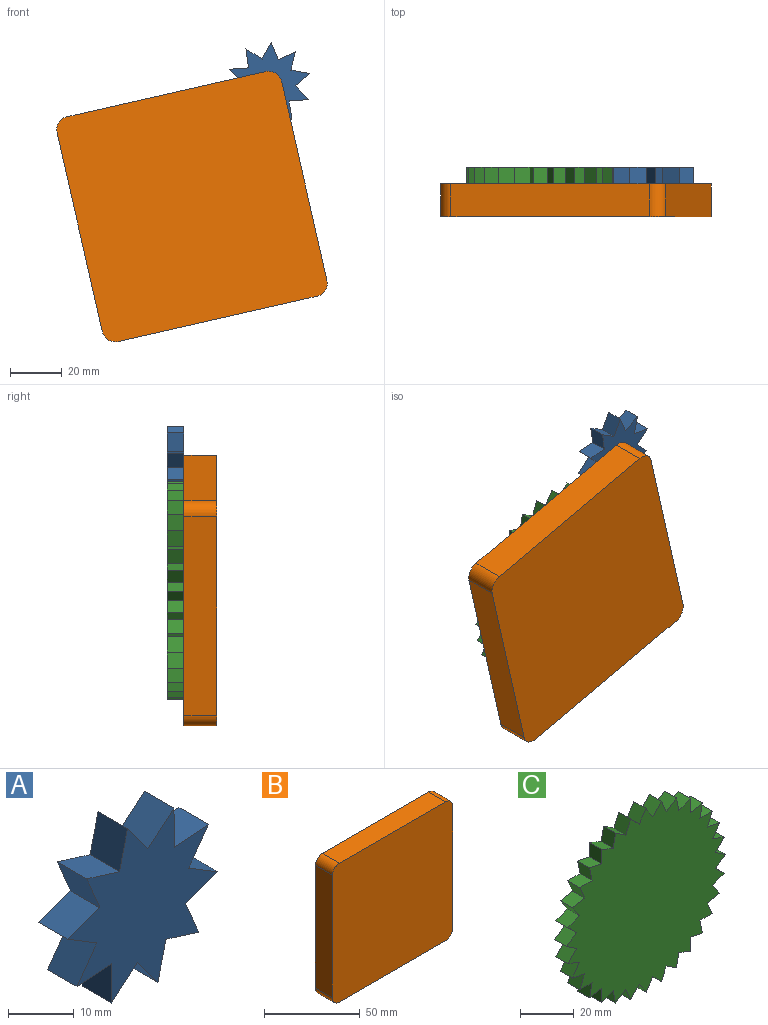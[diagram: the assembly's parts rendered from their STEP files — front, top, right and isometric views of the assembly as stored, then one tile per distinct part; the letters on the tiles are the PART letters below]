
ASSEMBLY  parts=3 mates=2
PART A: 22 faces, bbox 32.4x6.4x31.9 mm
  f0: plane 7.34x6.35mm, normal (0.08,0,-1), area 46.8mm2, adj f1,f19,f20,f21
  f1: plane 7.37x6.35mm, normal (-1,0,-0.01), area 46.8mm2, adj f0,f2,f20,f21
  f2: plane 6.35x5.61mm, normal (0.65,0,-0.76), area 46.8mm2, adj f1,f3,f20,f21
  f3: plane 6.35x5.9mm, normal (-0.8,0,-0.6), area 46.8mm2, adj f2,f4,f20,f21
  f4: plane 7.16x6.35mm, normal (0.97,0,-0.23), area 46.8mm2, adj f3,f5,f20,f21
  f5: plane 7.04x6.35mm, normal (-0.3,0,-0.96), area 46.8mm2, adj f4,f6,f20,f21
  f6: plane 6.81x6.35mm, normal (0.92,0,0.38), area 46.8mm2, adj f5,f7,f20,f21
  f7: plane 6.98x6.35mm, normal (0.32,0,-0.95), area 46.8mm2, adj f6,f8,f20,f21
  f8: plane 6.35x6.28mm, normal (0.52,0,0.85), area 46.8mm2, adj f7,f9,f20,f21
  f9: plane 6.35x6.02mm, normal (0.82,0,-0.58), area 46.8mm2, adj f8,f10,f20,f21
  f10: plane 7.34x6.35mm, normal (-0.08,0,1), area 46.8mm2, adj f9,f11,f20,f21
  f11: plane 7.37x6.35mm, normal (1,0,0.01), area 46.8mm2, adj f10,f12,f20,f21
  f12: plane 6.35x5.61mm, normal (-0.65,0,0.76), area 46.8mm2, adj f11,f13,f20,f21
  f13: plane 6.35x5.9mm, normal (0.8,0,0.6), area 46.8mm2, adj f12,f14,f20,f21
  f14: plane 7.16x6.35mm, normal (-0.97,0,0.23), area 46.8mm2, adj f13,f15,f20,f21
  f15: plane 7.04x6.35mm, normal (0.3,0,0.96), area 46.8mm2, adj f14,f16,f20,f21
  f16: plane 6.81x6.35mm, normal (-0.92,0,-0.38), area 46.8mm2, adj f15,f17,f20,f21
  f17: plane 6.98x6.35mm, normal (-0.32,0,0.95), area 46.8mm2, adj f16,f18,f20,f21
  f18: plane 6.35x6.28mm, normal (-0.52,0,-0.85), area 46.8mm2, adj f17,f19,f20,f21
  f19: plane 6.35x6.02mm, normal (-0.82,0,0.58), area 46.8mm2, adj f0,f18,f20,f21
  f20: plane 32.4x31.94mm, normal (0,-1,0), area 510.3mm2, adj f0,f1,f2,f3,f4,f5,f6,f7
  f21: plane 32.4x31.94mm, normal (0,1,0), area 510.3mm2, adj f0,f1,f2,f3,f4,f5,f6,f7
PART B: 10 faces, bbox 88.9x12.7x88.9 mm
  f0: plane 78.74x12.7mm, normal (-1,0,0), area 1000mm2, adj f4,f5,f6,f8
  f1: plane 78.74x12.7mm, normal (0,0,-1), area 1000mm2, adj f4,f5,f8,f9
  f2: plane 78.74x12.7mm, normal (1,0,0), area 1000mm2, adj f4,f5,f7,f9
  f3: plane 78.74x12.7mm, normal (0,0,1), area 1000mm2, adj f4,f5,f6,f7
  f4: plane 88.9x88.9mm, normal (0,-1,0), area 7881.1mm2, adj f0,f1,f2,f3,f6,f7,f8,f9
  f5: plane 88.9x88.9mm, normal (0,1,0), area 7881.1mm2, adj f0,f1,f2,f3,f6,f7,f8,f9
  f6: cylinder r=5.08mm len=12.7mm, axis (0,-1,0), area 101.3mm2, adj f0,f3,f4,f5
  f7: cylinder r=5.08mm len=12.7mm, axis (0,1,0), area 101.3mm2, adj f2,f3,f4,f5
  f8: cylinder r=5.08mm len=12.7mm, axis (0,1,0), area 101.3mm2, adj f0,f1,f4,f5
  f9: cylinder r=5.08mm len=12.7mm, axis (0,-1,0), area 101.3mm2, adj f1,f2,f4,f5
PART C: 66 faces, bbox 84.2x6.4x84.2 mm
  f0: plane 6.5x6.35mm, normal (-1,0,0), area 41.3mm2, adj f1,f63,f64,f65
  f1: plane 6.38x6.35mm, normal (0.2,0,0.98), area 41.3mm2, adj f0,f2,f64,f65
  f2: plane 6.38x6.35mm, normal (-0.98,0,-0.2), area 41.3mm2, adj f1,f3,f64,f65
  f3: plane 6.5x6.35mm, normal (0,0,1), area 41.3mm2, adj f2,f4,f64,f65
  f4: plane 6.35x6.01mm, normal (-0.92,0,-0.38), area 41.3mm2, adj f3,f5,f64,f65
  f5: plane 6.38x6.35mm, normal (-0.2,0,0.98), area 41.3mm2, adj f4,f6,f64,f65
  f6: plane 6.35x5.41mm, normal (-0.83,0,-0.56), area 41.3mm2, adj f5,f7,f64,f65
  f7: plane 6.35x6.01mm, normal (-0.38,0,0.92), area 41.3mm2, adj f6,f8,f64,f65
  f8: plane 6.35x4.6mm, normal (-0.71,0,-0.71), area 41.3mm2, adj f7,f9,f64,f65
  f9: plane 6.35x5.41mm, normal (-0.56,0,0.83), area 41.3mm2, adj f8,f10,f64,f65
  f10: plane 6.35x5.41mm, normal (-0.56,0,-0.83), area 41.3mm2, adj f9,f11,f64,f65
  f11: plane 6.35x4.6mm, normal (-0.71,0,0.71), area 41.3mm2, adj f10,f12,f64,f65
  f12: plane 6.35x6.01mm, normal (-0.38,0,-0.92), area 41.3mm2, adj f11,f13,f64,f65
  f13: plane 6.35x5.41mm, normal (-0.83,0,0.56), area 41.3mm2, adj f12,f14,f64,f65
  f14: plane 6.38x6.35mm, normal (-0.2,0,-0.98), area 41.3mm2, adj f13,f15,f64,f65
  f15: plane 6.35x6.01mm, normal (-0.92,0,0.38), area 41.3mm2, adj f14,f16,f64,f65
  f16: plane 6.5x6.35mm, normal (0,0,-1), area 41.3mm2, adj f15,f17,f64,f65
  f17: plane 6.38x6.35mm, normal (-0.98,0,0.2), area 41.3mm2, adj f16,f18,f64,f65
  f18: plane 6.38x6.35mm, normal (0.2,0,-0.98), area 41.3mm2, adj f17,f19,f64,f65
  f19: plane 6.5x6.35mm, normal (-1,0,0), area 41.3mm2, adj f18,f20,f64,f65
  f20: plane 6.35x6.01mm, normal (0.38,0,-0.92), area 41.3mm2, adj f19,f21,f64,f65
  f21: plane 6.38x6.35mm, normal (-0.98,0,-0.2), area 41.3mm2, adj f20,f22,f64,f65
  f22: plane 6.35x5.41mm, normal (0.56,0,-0.83), area 41.3mm2, adj f21,f23,f64,f65
  f23: plane 6.35x6.01mm, normal (-0.92,0,-0.38), area 41.3mm2, adj f22,f24,f64,f65
  f24: plane 6.35x4.6mm, normal (0.71,0,-0.71), area 41.3mm2, adj f23,f25,f64,f65
  f25: plane 6.35x5.41mm, normal (-0.83,0,-0.56), area 41.3mm2, adj f24,f26,f64,f65
  f26: plane 6.35x5.41mm, normal (0.83,0,-0.56), area 41.3mm2, adj f25,f27,f64,f65
  f27: plane 6.35x4.6mm, normal (-0.71,0,-0.71), area 41.3mm2, adj f26,f28,f64,f65
  f28: plane 6.35x6.01mm, normal (0.92,0,-0.38), area 41.3mm2, adj f27,f29,f64,f65
  f29: plane 6.35x5.41mm, normal (-0.56,0,-0.83), area 41.3mm2, adj f28,f30,f64,f65
  f30: plane 6.38x6.35mm, normal (0.98,0,-0.2), area 41.3mm2, adj f29,f31,f64,f65
  f31: plane 6.35x6.01mm, normal (-0.38,0,-0.92), area 41.3mm2, adj f30,f32,f64,f65
  f32: plane 6.5x6.35mm, normal (1,0,0), area 41.3mm2, adj f31,f33,f64,f65
  f33: plane 6.38x6.35mm, normal (-0.2,0,-0.98), area 41.3mm2, adj f32,f34,f64,f65
  f34: plane 6.38x6.35mm, normal (0.98,0,0.2), area 41.3mm2, adj f33,f35,f64,f65
  f35: plane 6.5x6.35mm, normal (0,0,-1), area 41.3mm2, adj f34,f36,f64,f65
  f36: plane 6.35x6.01mm, normal (0.92,0,0.38), area 41.3mm2, adj f35,f37,f64,f65
  f37: plane 6.38x6.35mm, normal (0.2,0,-0.98), area 41.3mm2, adj f36,f38,f64,f65
  f38: plane 6.35x5.41mm, normal (0.83,0,0.56), area 41.3mm2, adj f37,f39,f64,f65
  f39: plane 6.35x6.01mm, normal (0.38,0,-0.92), area 41.3mm2, adj f38,f40,f64,f65
  f40: plane 6.35x4.6mm, normal (0.71,0,0.71), area 41.3mm2, adj f39,f41,f64,f65
  f41: plane 6.35x5.41mm, normal (0.56,0,-0.83), area 41.3mm2, adj f40,f42,f64,f65
  f42: plane 6.35x5.41mm, normal (0.56,0,0.83), area 41.3mm2, adj f41,f43,f64,f65
  f43: plane 6.35x4.6mm, normal (0.71,0,-0.71), area 41.3mm2, adj f42,f44,f64,f65
  f44: plane 6.35x6.01mm, normal (0.38,0,0.92), area 41.3mm2, adj f43,f45,f64,f65
  f45: plane 6.35x5.41mm, normal (0.83,0,-0.56), area 41.3mm2, adj f44,f46,f64,f65
  f46: plane 6.38x6.35mm, normal (0.2,0,0.98), area 41.3mm2, adj f45,f47,f64,f65
  f47: plane 6.35x6.01mm, normal (0.92,0,-0.38), area 41.3mm2, adj f46,f48,f64,f65
  f48: plane 6.5x6.35mm, normal (0,0,1), area 41.3mm2, adj f47,f49,f64,f65
  f49: plane 6.38x6.35mm, normal (0.98,0,-0.2), area 41.3mm2, adj f48,f50,f64,f65
  f50: plane 6.38x6.35mm, normal (-0.2,0,0.98), area 41.3mm2, adj f49,f51,f64,f65
  f51: plane 6.5x6.35mm, normal (1,0,0), area 41.3mm2, adj f50,f52,f64,f65
  f52: plane 6.35x6.01mm, normal (-0.38,0,0.92), area 41.3mm2, adj f51,f53,f64,f65
  f53: plane 6.38x6.35mm, normal (0.98,0,0.2), area 41.3mm2, adj f52,f54,f64,f65
  f54: plane 6.35x5.41mm, normal (-0.56,0,0.83), area 41.3mm2, adj f53,f55,f64,f65
  f55: plane 6.35x6.01mm, normal (0.92,0,0.38), area 41.3mm2, adj f54,f56,f64,f65
  f56: plane 6.35x4.6mm, normal (-0.71,0,0.71), area 41.3mm2, adj f55,f57,f64,f65
  f57: plane 6.35x5.41mm, normal (0.83,0,0.56), area 41.3mm2, adj f56,f58,f64,f65
  f58: plane 6.35x5.41mm, normal (-0.83,0,0.56), area 41.3mm2, adj f57,f59,f64,f65
  f59: plane 6.35x4.68mm, normal (0.72,0,0.69), area 41.3mm2, adj f58,f60,f64,f65
  f60: plane 6.35x6.09mm, normal (-0.92,0,0.39), area 42mm2, adj f59,f61,f64,f65
  f61: plane 6.35x5.41mm, normal (0.56,0,0.83), area 41.3mm2, adj f60,f62,f64,f65
  f62: plane 6.38x6.35mm, normal (-0.98,0,0.2), area 41.3mm2, adj f61,f63,f64,f65
  f63: plane 6.35x6.01mm, normal (0.38,0,0.92), area 41.3mm2, adj f0,f62,f64,f65
  f64: plane 84.17x84.17mm, normal (0,-1,0), area 4865.4mm2, adj f0,f1,f2,f3,f4,f5,f6,f7
  f65: plane 84.17x84.17mm, normal (0,1,0), area 4865.4mm2, adj f0,f1,f2,f3,f4,f5,f6,f7
PLACE A rot(axis=(1,0,0.07),180deg) t=(116.52,-12.7,100.97)mm
PLACE B rot(axis=(0.99,0,0.11),180deg) t=(87.23,-25.4,53)mm fixed
PLACE C rot(axis=(0.98,0,-0.19),180deg) t=(87.23,-9.53,53.01)mm
MATE revolute B.f9 <-> A.f21  axis (0,1,0) through (116.89,-12.7,100.12)mm
MATE revolute B.f4 <-> C.f65  axis (0,1,0) through (87.23,-12.7,53)mm
